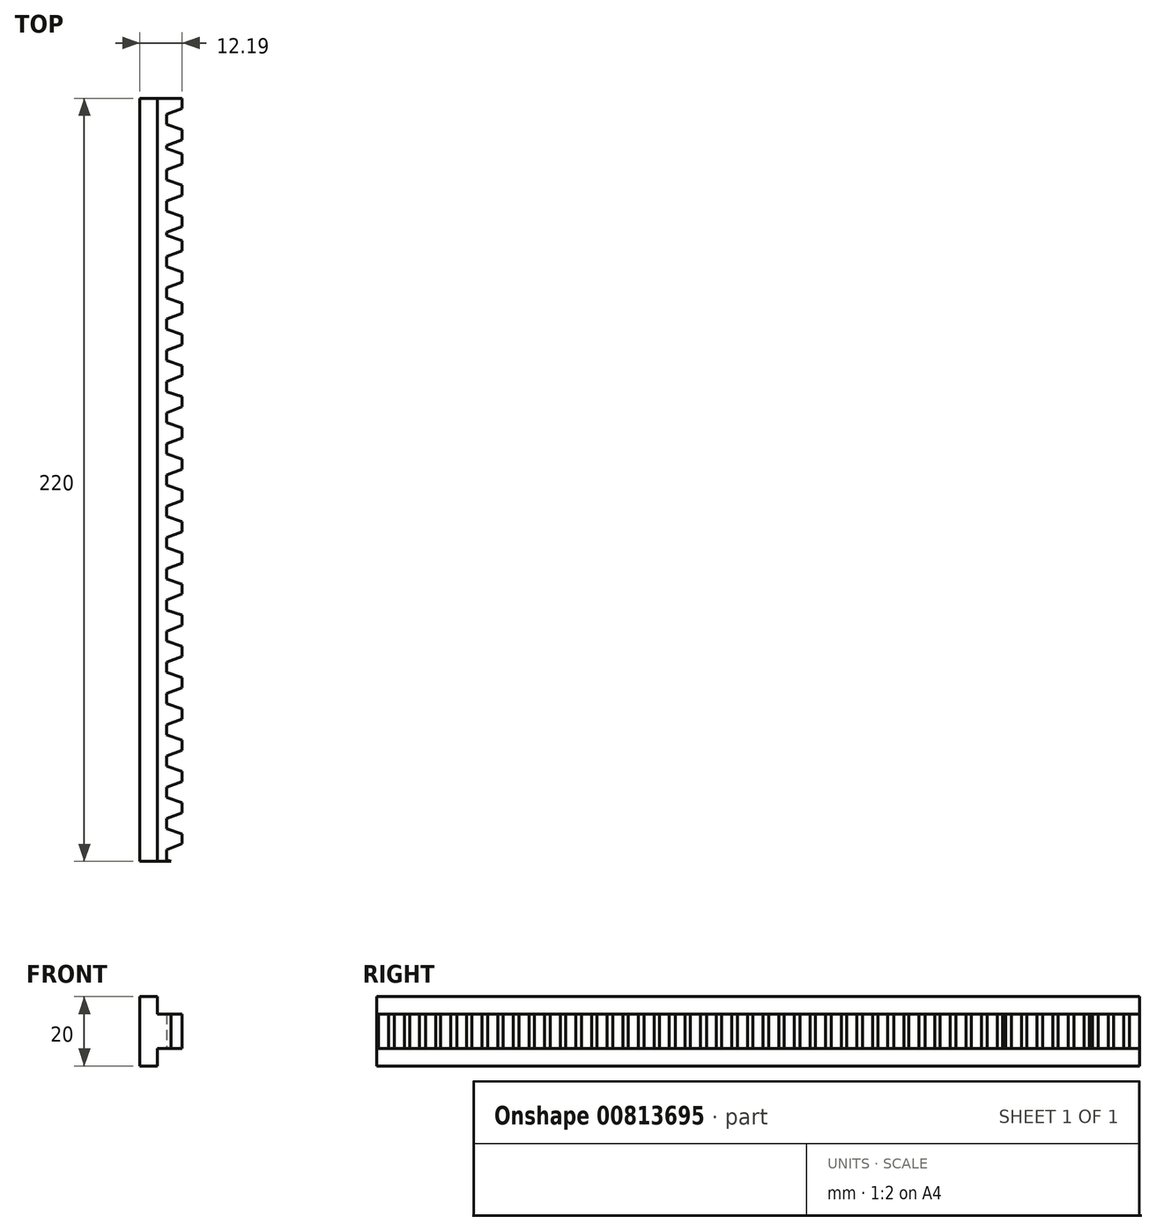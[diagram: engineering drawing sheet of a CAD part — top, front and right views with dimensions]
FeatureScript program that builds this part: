
annotation { "Feature Type Name" : "Feature", "Feature Type Description" : "" }
export const myFeature = defineFeature(function(context is Context, id is Id, definition is map)
    precondition{}
    {
        {
            var Q0;
            Q0=qCreatedBy(makeId("Top.planeOp"),FACE);
            var sketch = newSketch(context, id + "F0", { "sketchPlane" : qUnion([Q0])});
            skLineSegment(sketch, "E0", {"start": v(0, 114.44) * mm, "end": v(0, -105.56) * mm});
            skLineSegment(sketch, "E1", {"start": v(0, -105.56) * mm, "end": v(4.03, -105.56) * mm});
            skLineSegment(sketch, "E2", {"start": v(2.7, 50.8) * mm, "end": v(7.2, 52.48) * mm});
            skLineSegment(sketch, "E3", {"start": v(7.2, 52.48) * mm, "end": v(7.2, 55.38) * mm});
            skLineSegment(sketch, "E4", {"start": v(7.2, 55.38) * mm, "end": v(2.7, 56.9) * mm});
            skLineSegment(sketch, "E5", {"start": v(2.7, 56.9) * mm, "end": v(2.7, 59.8) * mm});
            skLineSegment(sketch, "E6", {"start": v(2.7, 50.8) * mm, "end": v(2.7, 47.9) * mm});
            skLineSegment(sketch, "E7.1.0.0", {"start": v(7.2, 46.38) * mm, "end": v(2.7, 47.9) * mm});
            skLineSegment(sketch, "E7.1.0.1", {"start": v(7.2, 43.48) * mm, "end": v(7.2, 46.38) * mm});
            skLineSegment(sketch, "E7.1.0.2", {"start": v(2.7, 41.8) * mm, "end": v(7.2, 43.48) * mm});
            skLineSegment(sketch, "E7.1.0.3", {"start": v(2.7, 47.9) * mm, "end": v(2.7, 50.8) * mm});
            skLineSegment(sketch, "E7.2.0.0", {"start": v(7.2, 37.38) * mm, "end": v(2.7, 38.9) * mm});
            skLineSegment(sketch, "E7.2.0.1", {"start": v(7.2, 34.48) * mm, "end": v(7.2, 37.38) * mm});
            skLineSegment(sketch, "E7.2.0.2", {"start": v(2.7, 32.8) * mm, "end": v(7.2, 34.48) * mm});
            skLineSegment(sketch, "E7.2.0.3", {"start": v(2.7, 38.9) * mm, "end": v(2.7, 41.8) * mm});
            skLineSegment(sketch, "E7.3.0.0", {"start": v(7.2, 28.38) * mm, "end": v(2.7, 29.9) * mm});
            skLineSegment(sketch, "E7.3.0.1", {"start": v(7.2, 25.48) * mm, "end": v(7.2, 28.38) * mm});
            skLineSegment(sketch, "E7.3.0.2", {"start": v(2.7, 23.8) * mm, "end": v(7.2, 25.48) * mm});
            skLineSegment(sketch, "E7.3.0.3", {"start": v(2.7, 29.9) * mm, "end": v(2.7, 32.8) * mm});
            skLineSegment(sketch, "E7.4.0.0", {"start": v(7.2, 19.38) * mm, "end": v(2.7, 20.9) * mm});
            skLineSegment(sketch, "E7.4.0.1", {"start": v(7.2, 16.48) * mm, "end": v(7.2, 19.38) * mm});
            skLineSegment(sketch, "E7.4.0.2", {"start": v(2.7, 14.8) * mm, "end": v(7.2, 16.48) * mm});
            skLineSegment(sketch, "E7.4.0.3", {"start": v(2.7, 20.9) * mm, "end": v(2.7, 23.8) * mm});
            skLineSegment(sketch, "E7.5.0.0", {"start": v(7.2, 10.38) * mm, "end": v(2.7, 11.9) * mm});
            skLineSegment(sketch, "E7.5.0.1", {"start": v(7.2, 7.48) * mm, "end": v(7.2, 10.38) * mm});
            skLineSegment(sketch, "E7.5.0.2", {"start": v(2.7, 5.8) * mm, "end": v(7.2, 7.48) * mm});
            skLineSegment(sketch, "E7.5.0.3", {"start": v(2.7, 11.9) * mm, "end": v(2.7, 14.8) * mm});
            skLineSegment(sketch, "E7.6.0.0", {"start": v(7.2, 1.38) * mm, "end": v(2.7, 2.9) * mm});
            skLineSegment(sketch, "E7.6.0.1", {"start": v(7.2, -1.52) * mm, "end": v(7.2, 1.38) * mm});
            skLineSegment(sketch, "E7.6.0.2", {"start": v(2.7, -3.2) * mm, "end": v(7.2, -1.52) * mm});
            skLineSegment(sketch, "E7.6.0.3", {"start": v(2.7, 2.9) * mm, "end": v(2.7, 5.8) * mm});
            skLineSegment(sketch, "E7.7.0.0", {"start": v(7.2, -7.62) * mm, "end": v(2.7, -6.1) * mm});
            skLineSegment(sketch, "E7.7.0.1", {"start": v(7.2, -10.52) * mm, "end": v(7.2, -7.62) * mm});
            skLineSegment(sketch, "E7.7.0.2", {"start": v(2.7, -12.2) * mm, "end": v(7.2, -10.52) * mm});
            skLineSegment(sketch, "E7.7.0.3", {"start": v(2.7, -6.1) * mm, "end": v(2.7, -3.2) * mm});
            skLineSegment(sketch, "E7.8.0.0", {"start": v(7.2, -16.62) * mm, "end": v(2.7, -15.1) * mm});
            skLineSegment(sketch, "E7.8.0.1", {"start": v(7.2, -19.52) * mm, "end": v(7.2, -16.62) * mm});
            skLineSegment(sketch, "E7.8.0.2", {"start": v(2.7, -21.2) * mm, "end": v(7.2, -19.52) * mm});
            skLineSegment(sketch, "E7.8.0.3", {"start": v(2.7, -15.1) * mm, "end": v(2.7, -12.2) * mm});
            skLineSegment(sketch, "E7.9.0.0", {"start": v(7.2, -25.62) * mm, "end": v(2.7, -24.1) * mm});
            skLineSegment(sketch, "E7.9.0.1", {"start": v(7.2, -28.52) * mm, "end": v(7.2, -25.62) * mm});
            skLineSegment(sketch, "E7.9.0.2", {"start": v(2.7, -30.2) * mm, "end": v(7.2, -28.52) * mm});
            skLineSegment(sketch, "E7.9.0.3", {"start": v(2.7, -24.1) * mm, "end": v(2.7, -21.2) * mm});
            skLineSegment(sketch, "E7.10.0.0", {"start": v(7.2, -34.62) * mm, "end": v(2.7, -33.1) * mm});
            skLineSegment(sketch, "E7.10.0.1", {"start": v(7.2, -37.52) * mm, "end": v(7.2, -34.62) * mm});
            skLineSegment(sketch, "E7.10.0.2", {"start": v(2.7, -39.2) * mm, "end": v(7.2, -37.52) * mm});
            skLineSegment(sketch, "E7.10.0.3", {"start": v(2.7, -33.1) * mm, "end": v(2.7, -30.2) * mm});
            skLineSegment(sketch, "E7.11.0.0", {"start": v(7.2, -43.62) * mm, "end": v(2.7, -42.1) * mm});
            skLineSegment(sketch, "E7.11.0.1", {"start": v(7.2, -46.52) * mm, "end": v(7.2, -43.62) * mm});
            skLineSegment(sketch, "E7.11.0.2", {"start": v(2.7, -48.2) * mm, "end": v(7.2, -46.52) * mm});
            skLineSegment(sketch, "E7.11.0.3", {"start": v(2.7, -42.1) * mm, "end": v(2.7, -39.2) * mm});
            skLineSegment(sketch, "E7.12.0.0", {"start": v(7.2, -52.62) * mm, "end": v(2.7, -51.1) * mm});
            skLineSegment(sketch, "E7.12.0.1", {"start": v(7.2, -55.52) * mm, "end": v(7.2, -52.62) * mm});
            skLineSegment(sketch, "E7.12.0.2", {"start": v(2.7, -57.2) * mm, "end": v(7.2, -55.52) * mm});
            skLineSegment(sketch, "E7.12.0.3", {"start": v(2.7, -51.1) * mm, "end": v(2.7, -48.2) * mm});
            skLineSegment(sketch, "E7.13.0.0", {"start": v(7.2, -61.62) * mm, "end": v(2.7, -60.1) * mm});
            skLineSegment(sketch, "E7.13.0.1", {"start": v(7.2, -64.52) * mm, "end": v(7.2, -61.62) * mm});
            skLineSegment(sketch, "E7.13.0.2", {"start": v(2.7, -66.2) * mm, "end": v(7.2, -64.52) * mm});
            skLineSegment(sketch, "E7.13.0.3", {"start": v(2.7, -60.1) * mm, "end": v(2.7, -57.2) * mm});
            skLineSegment(sketch, "E7.14.0.0", {"start": v(7.2, -70.62) * mm, "end": v(2.7, -69.1) * mm});
            skLineSegment(sketch, "E7.14.0.1", {"start": v(7.2, -73.52) * mm, "end": v(7.2, -70.62) * mm});
            skLineSegment(sketch, "E7.14.0.2", {"start": v(2.7, -75.2) * mm, "end": v(7.2, -73.52) * mm});
            skLineSegment(sketch, "E7.14.0.3", {"start": v(2.7, -69.1) * mm, "end": v(2.7, -66.2) * mm});
            skLineSegment(sketch, "E7.15.0.0", {"start": v(7.2, -79.62) * mm, "end": v(2.7, -78.1) * mm});
            skLineSegment(sketch, "E7.15.0.1", {"start": v(7.2, -82.52) * mm, "end": v(7.2, -79.62) * mm});
            skLineSegment(sketch, "E7.15.0.2", {"start": v(2.7, -84.2) * mm, "end": v(7.2, -82.52) * mm});
            skLineSegment(sketch, "E7.15.0.3", {"start": v(2.7, -78.1) * mm, "end": v(2.7, -75.2) * mm});
            skLineSegment(sketch, "E7.16.0.0", {"start": v(7.2, -88.62) * mm, "end": v(2.7, -87.1) * mm});
            skLineSegment(sketch, "E7.16.0.1", {"start": v(7.2, -91.52) * mm, "end": v(7.2, -88.62) * mm});
            skLineSegment(sketch, "E7.16.0.2", {"start": v(2.7, -93.2) * mm, "end": v(7.2, -91.52) * mm});
            skLineSegment(sketch, "E7.16.0.3", {"start": v(2.7, -87.1) * mm, "end": v(2.7, -84.2) * mm});
            skLineSegment(sketch, "E7.17.0.0", {"start": v(7.2, -97.62) * mm, "end": v(2.7, -96.1) * mm});
            skLineSegment(sketch, "E7.17.0.1", {"start": v(7.2, -100.52) * mm, "end": v(7.2, -97.62) * mm});
            skLineSegment(sketch, "E7.17.0.2", {"start": v(2.7, -102.2) * mm, "end": v(7.2, -100.52) * mm});
            skLineSegment(sketch, "E7.17.0.3", {"start": v(2.7, -96.1) * mm, "end": v(2.7, -93.2) * mm});
            skLineSegment(sketch, "E7.18.0.0", {"start": v(4.03, -105.56) * mm, "end": v(2.7, -105.1) * mm});
            skLineSegment(sketch, "E7.18.0.3", {"start": v(2.7, -105.1) * mm, "end": v(2.7, -102.2) * mm});
            skLineSegment(sketch, "E7.direction1", {"start": v(2.7, 50.8) * mm, "end": v(2.7, 41.8) * mm, "construction": true});
            skLineSegment(sketch, "E8", {"start": v(2.7, 114.44) * mm, "end": v(2.7, -105.56) * mm, "construction": true});
            skLineSegment(sketch, "E9.0.1.0", {"start": v(2.7, 75.8) * mm, "end": v(7.2, 77.48) * mm});
            skLineSegment(sketch, "E9.0.1.1", {"start": v(7.2, 77.48) * mm, "end": v(7.2, 80.38) * mm});
            skLineSegment(sketch, "E9.0.1.2", {"start": v(7.2, 80.38) * mm, "end": v(2.7, 81.9) * mm});
            skLineSegment(sketch, "E9.0.1.3", {"start": v(2.7, 81.9) * mm, "end": v(2.7, 84.8) * mm});
            skLineSegment(sketch, "E9.0.2.0", {"start": v(2.7, 100.8) * mm, "end": v(7.2, 102.48) * mm});
            skLineSegment(sketch, "E9.0.2.1", {"start": v(7.2, 102.48) * mm, "end": v(7.2, 105.38) * mm});
            skLineSegment(sketch, "E9.0.2.2", {"start": v(7.2, 105.38) * mm, "end": v(2.7, 106.9) * mm});
            skLineSegment(sketch, "E9.0.2.3", {"start": v(2.7, 106.9) * mm, "end": v(2.7, 109.8) * mm});
            skLineSegment(sketch, "E9.1.0.0", {"start": v(2.7, 59.8) * mm, "end": v(7.2, 61.48) * mm});
            skLineSegment(sketch, "E9.1.0.1", {"start": v(7.2, 61.48) * mm, "end": v(7.2, 64.38) * mm});
            skLineSegment(sketch, "E9.1.0.2", {"start": v(7.2, 64.38) * mm, "end": v(2.7, 65.9) * mm});
            skLineSegment(sketch, "E9.1.0.3", {"start": v(2.7, 65.9) * mm, "end": v(2.7, 68.8) * mm});
            skLineSegment(sketch, "E9.1.1.0", {"start": v(2.7, 84.8) * mm, "end": v(7.2, 86.48) * mm});
            skLineSegment(sketch, "E9.1.1.1", {"start": v(7.2, 86.48) * mm, "end": v(7.2, 89.38) * mm});
            skLineSegment(sketch, "E9.1.1.2", {"start": v(7.2, 89.38) * mm, "end": v(2.7, 90.9) * mm});
            skLineSegment(sketch, "E9.1.1.3", {"start": v(2.7, 90.9) * mm, "end": v(2.7, 93.8) * mm});
            skLineSegment(sketch, "E9.1.2.0", {"start": v(2.7, 109.8) * mm, "end": v(7.2, 111.48) * mm});
            skLineSegment(sketch, "E9.1.2.1", {"start": v(7.2, 111.48) * mm, "end": v(7.2, 114.38) * mm});
            skLineSegment(sketch, "E9.2.0.0", {"start": v(2.7, 68.8) * mm, "end": v(7.2, 70.48) * mm});
            skLineSegment(sketch, "E9.2.0.1", {"start": v(7.2, 70.48) * mm, "end": v(7.2, 73.38) * mm});
            skLineSegment(sketch, "E9.2.0.2", {"start": v(7.2, 73.38) * mm, "end": v(2.7, 74.9) * mm});
            skLineSegment(sketch, "E9.2.0.3", {"start": v(2.7, 74.9) * mm, "end": v(2.7, 77.8) * mm});
            skLineSegment(sketch, "E9.2.1.0", {"start": v(2.7, 93.8) * mm, "end": v(7.2, 95.48) * mm});
            skLineSegment(sketch, "E9.2.1.1", {"start": v(7.2, 95.48) * mm, "end": v(7.2, 98.38) * mm});
            skLineSegment(sketch, "E9.2.1.2", {"start": v(7.2, 98.38) * mm, "end": v(2.7, 99.9) * mm});
            skLineSegment(sketch, "E9.2.1.3", {"start": v(2.7, 99.9) * mm, "end": v(2.7, 102.8) * mm});
            skLineSegment(sketch, "E9.direction1", {"start": v(2.7, 50.8) * mm, "end": v(2.7, 59.8) * mm, "construction": true});
            skLineSegment(sketch, "E9.direction2", {"start": v(2.7, 50.8) * mm, "end": v(2.7, 75.8) * mm, "construction": true});
            skLineSegment(sketch, "E10", {"start": v(7.2, 114.38) * mm, "end": v(0, 114.44) * mm});
            skSolve(sketch);
        }
        {
            var Q0;
            Q0 = qSketchRegion(id + "F0", true);
            extrude(context, id + "F1", {"entities" : qUnion([Q0]), "depth" : 10 * mm, "offsetDistance" : 25 * mm});
        }
        {
            var Q0;
            Q0=makeQuery(id+"F1.opExtrude","SWEPT_FACE",FACE,{"disambiguationData":[OSD([sQuery(id+"F0.wireOp",EDGE,"E0")])]});
            var sketch = newSketch(context, id + "F2", { "sketchPlane" : qUnion([Q0])});
            skLineSegment(sketch, "E11", {"start": v(-114.44, 5) * mm, "end": v(-114.44, 15) * mm});
            skLineSegment(sketch, "E12", {"start": v(-114.44, 15) * mm, "end": v(105.56, 15) * mm});
            skLineSegment(sketch, "E13", {"start": v(105.56, 15) * mm, "end": v(105.56, 5) * mm});
            skLineSegment(sketch, "E14", {"start": v(105.56, 5) * mm, "end": v(-114.44, 5) * mm, "construction": true});
            skLineSegment(sketch, "E15.MirrorCS", {"start": v(-114.44, 5) * mm, "end": v(-114.44, -5) * mm});
            skLineSegment(sketch, "E16.MirrorCS", {"start": v(-114.44, -5) * mm, "end": v(105.56, -5) * mm});
            skLineSegment(sketch, "E17.MirrorCS", {"start": v(105.56, -5) * mm, "end": v(105.56, 5) * mm});
            skSolve(sketch);
        }
        {
            var Q0;
            Q0 = qSketchRegion(id + "F2", true);
            extrude(context, id + "F3", {"entities" : qUnion([Q0]), "operationType" : NewBodyOperationType.ADD, "depth" : 5 * mm, "offsetDistance" : 25 * mm});
        }
    });
